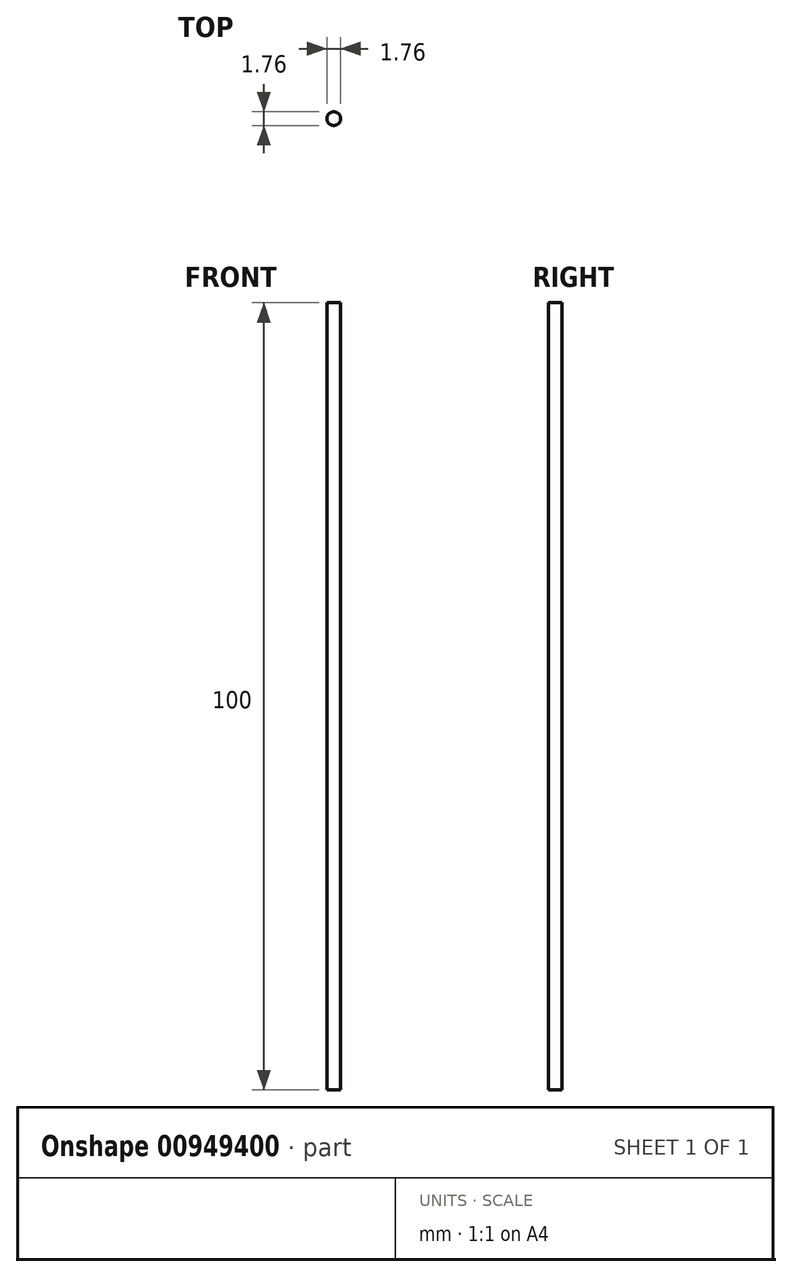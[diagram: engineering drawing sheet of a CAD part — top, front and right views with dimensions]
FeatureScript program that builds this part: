
annotation { "Feature Type Name" : "Feature", "Feature Type Description" : "" }
export const myFeature = defineFeature(function(context is Context, id is Id, definition is map)
    precondition{}
    {
        {
            var Q0;
            Q0=qCreatedBy(makeId("Top.planeOp"),FACE);
            var sketch = newSketch(context, id + "F0", { "sketchPlane" : qUnion([Q0])});
            skCircle(sketch, "E0", {"center": v(0, 0) * mm, "radius": 0.88 * mm});
            skSolve(sketch);
        }
        {
            var Q0;
            Q0=makeQuery(id+"F0.imprint","IMPRINT",FACE,{"disambiguationData":[TD([[makeQuery(id+"F0.imprint","IMPRINT",EDGE,{"derivedFrom":sQuery(id+"F0.wireOp",EDGE,"E0")}),1.0]])]});
            extrude(context, id + "F1", {"entities" : qUnion([Q0]), "depth" : 100 * mm, "offsetDistance" : 25 * mm});
        }
    });
